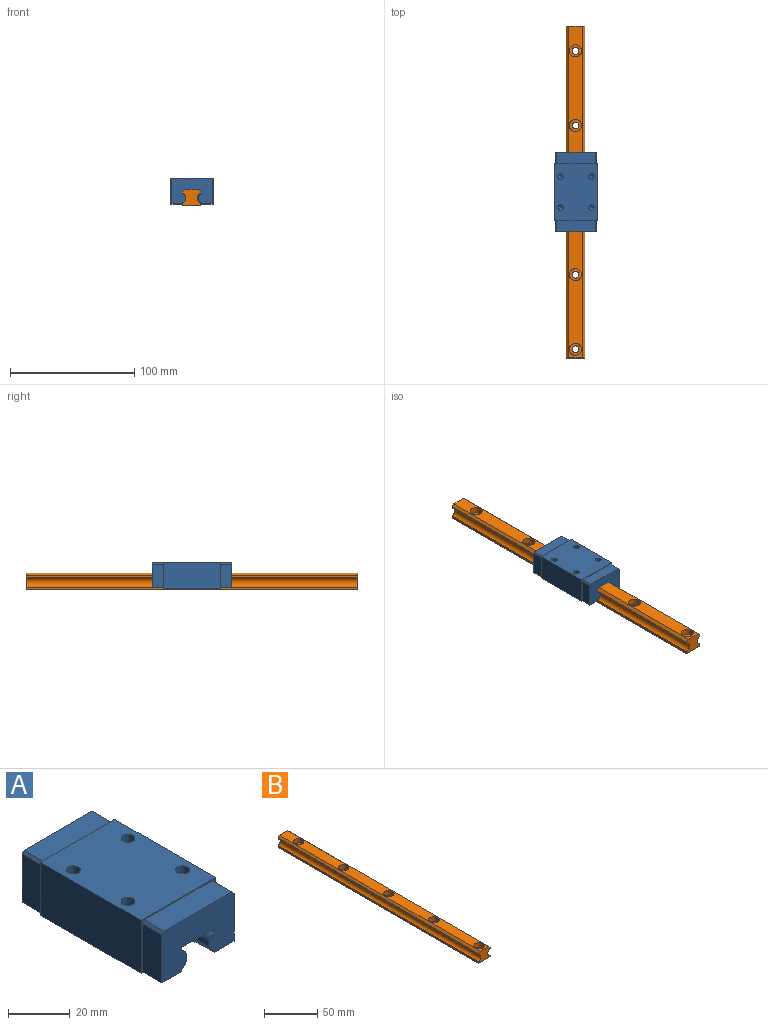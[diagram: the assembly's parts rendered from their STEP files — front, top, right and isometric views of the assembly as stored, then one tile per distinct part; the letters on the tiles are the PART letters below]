
ASSEMBLY  parts=2 mates=2
PART A: 38 faces, bbox 34x64x21 mm
  f0: plane 33x20mm, normal (0,1,0), area 543.3mm2, adj f6,f7,f9,f10,f11,f12,f13,f22
  f1: plane 46x9.5mm, normal (0,0,-1), area 437mm2, adj f2,f6,f21,f29
  f2: plane 46x21mm, normal (1,0,0), area 966mm2, adj f1,f3,f21,f29
  f3: plane 46x34mm, normal (0,0,1), area 1500.4mm2, adj f2,f4,f21,f29,f30,f32,f34,f36
  f4: plane 46x21mm, normal (-1,0,0), area 966mm2, adj f3,f5,f21,f29
  f5: plane 46x9.5mm, normal (0,0,-1), area 437mm2, adj f4,f7,f21,f29
  f6: plane 64x1.29mm, normal (-1,0,0), area 73.7mm2, adj f0,f1,f8,f10,f15,f21,f23,f29
  f7: plane 64x1.29mm, normal (1,0,0), area 73.7mm2, adj f0,f5,f8,f11,f14,f21,f22,f29
  f8: plane 33x20mm, normal (0,-1,0), area 543.3mm2, adj f6,f7,f9,f10,f11,f12,f13,f14
  f9: plane 64x1.29mm, normal (-1,0,0), area 82.7mm2, adj f0,f8,f10,f13
  f10: cylinder r=4mm len=64mm, axis (0,1,0), area 607.4mm2, adj f0,f6,f8,f9
  f11: cylinder r=4mm len=64mm, axis (0,1,0), area 607.4mm2, adj f0,f7,f8,f12
  f12: plane 64x1.29mm, normal (1,0,0), area 82.7mm2, adj f0,f8,f11,f13
  f13: plane 64x15mm, normal (0,0,-1), area 960mm2, adj f0,f8,f9,f12
  f14: plane 9x9mm, normal (0,0,-1), area 81mm2, adj f7,f8,f16,f21
  f15: plane 9x9mm, normal (0,0,-1), area 81mm2, adj f6,f8,f20,f21
  f16: plane 19x9mm, normal (-1,0,0), area 171mm2, adj f8,f14,f17,f21
  f17: plane 9x1mm, normal (-0.71,0,0.71), area 12.7mm2, adj f8,f16,f18,f21
  f18: plane 31x9mm, normal (0,0,1), area 279mm2, adj f8,f17,f19,f21
  f19: plane 9x1mm, normal (0.71,0,0.71), area 12.7mm2, adj f8,f18,f20,f21
  f20: plane 19x9mm, normal (1,0,0), area 171mm2, adj f8,f15,f19,f21
  f21: plane 34x21mm, normal (0,-1,0), area 47.5mm2, adj f1,f2,f3,f4,f5,f6,f7,f14
  f22: plane 9x9mm, normal (0,0,-1), area 81mm2, adj f0,f7,f28,f29
  f23: plane 9x9mm, normal (0,0,-1), area 81mm2, adj f0,f6,f24,f29
  f24: plane 19x9mm, normal (1,0,0), area 171mm2, adj f0,f23,f25,f29
  f25: plane 9x1mm, normal (0.71,0,0.71), area 12.7mm2, adj f0,f24,f26,f29
  f26: plane 31x9mm, normal (0,0,1), area 279mm2, adj f0,f25,f27,f29
  f27: plane 9x1mm, normal (-0.71,0,0.71), area 12.7mm2, adj f0,f26,f28,f29
  f28: plane 19x9mm, normal (-1,0,0), area 171mm2, adj f0,f22,f27,f29
  f29: plane 34x21mm, normal (0,1,0), area 47.5mm2, adj f1,f2,f3,f4,f5,f6,f7,f22
  f30: cylinder r=2.25mm len=10.4mm, axis (0,0,1), area 147mm2, adj f3,f31
  f31: cone r=0mm half-angle=59deg, axis (0,0,1), area 18.6mm2, adj f30
  f32: cylinder r=2.25mm len=10.4mm, axis (0,0,1), area 147mm2, adj f3,f33
  f33: cone r=0mm half-angle=59deg, axis (0,0,1), area 18.6mm2, adj f32
  f34: cylinder r=2.25mm len=10.4mm, axis (0,0,1), area 147mm2, adj f3,f35
  f35: cone r=0mm half-angle=59deg, axis (0,0,1), area 18.6mm2, adj f34
  f36: cylinder r=2.25mm len=10.4mm, axis (0,0,1), area 147mm2, adj f3,f37
  f37: cone r=0mm half-angle=59deg, axis (0,0,1), area 18.6mm2, adj f36
PART B: 27 faces, bbox 15x267x13.2 mm
  f0: plane 267x15mm, normal (0,0,-1), area 3886.2mm2, adj f5,f6,f10,f11,f14,f17,f20,f23
  f1: plane 267x11mm, normal (0,0,1), area 2563.7mm2, adj f2,f9,f10,f13,f16,f19,f22,f25
  f2: plane 267x2mm, normal (-0.71,0,0.71), area 755.2mm2, adj f1,f3,f10,f26
  f3: plane 267x1.35mm, normal (-1,0,0), area 360.8mm2, adj f2,f4,f10,f26
  f4: cylinder r=4mm len=267mm, axis (0,1,0), area 2765.7mm2, adj f3,f5,f10,f26
  f5: plane 267x2.15mm, normal (-1,0,0), area 574.4mm2, adj f0,f4,f10,f26
  f6: plane 267x2.15mm, normal (1,0,0), area 574.4mm2, adj f0,f7,f10,f26
  f7: cylinder r=4mm len=267mm, axis (0,1,0), area 2765.7mm2, adj f6,f8,f10,f26
  f8: plane 267x1.35mm, normal (1,0,0), area 360.8mm2, adj f7,f9,f10,f26
  f9: plane 267x2mm, normal (0.71,0,0.71), area 755.2mm2, adj f1,f8,f10,f26
  f10: plane 15x13.2mm, normal (0,1,0), area 161mm2, adj f0,f1,f2,f3,f4,f5,f6,f7
  f11: cylinder r=2.75mm len=8.2mm, axis (0,0,1), area 141.7mm2, adj f0,f12
  f12: plane 9.75x9.75mm, normal (0,0,1), area 50.9mm2, adj f11,f13
  f13: cylinder r=4.88mm len=9.75mm, axis (0,0,1), area 153.2mm2, adj f1,f12
  f14: cylinder r=2.75mm len=8.2mm, axis (0,0,1), area 141.7mm2, adj f0,f15
  f15: plane 9.75x9.75mm, normal (0,0,1), area 50.9mm2, adj f14,f16
  f16: cylinder r=4.88mm len=9.75mm, axis (0,0,1), area 153.2mm2, adj f1,f15
  f17: cylinder r=2.75mm len=8.2mm, axis (0,0,1), area 141.7mm2, adj f0,f18
  f18: plane 9.75x9.75mm, normal (0,0,1), area 50.9mm2, adj f17,f19
  f19: cylinder r=4.88mm len=9.75mm, axis (0,0,1), area 153.2mm2, adj f1,f18
  f20: cylinder r=2.75mm len=8.2mm, axis (0,0,1), area 141.7mm2, adj f0,f21
  f21: plane 9.75x9.75mm, normal (0,0,1), area 50.9mm2, adj f20,f22
  f22: cylinder r=4.88mm len=9.75mm, axis (0,0,1), area 153.2mm2, adj f1,f21
  f23: cylinder r=2.75mm len=8.2mm, axis (0,0,1), area 141.7mm2, adj f0,f24
  f24: plane 9.75x9.75mm, normal (0,0,1), area 50.9mm2, adj f23,f25
  f25: cylinder r=4.88mm len=9.75mm, axis (0,0,1), area 153.2mm2, adj f1,f24
  f26: plane 15x13.2mm, normal (0,-1,0), area 161mm2, adj f0,f1,f2,f3,f4,f5,f6,f7
PLACE A t=(0.41,-133.5,1)mm
PLACE B at identity fixed
MATE parallel B.f11 <-> A.f13  axis (0,0,1) through (0,-20,13.2)mm
MATE cylindrical A.f11 <-> B.f4  axis (0,1,0) through (-8.59,-133.5,6)mm
